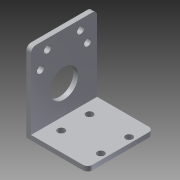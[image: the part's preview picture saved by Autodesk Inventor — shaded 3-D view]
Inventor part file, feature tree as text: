
AUTODESK INVENTOR PART (.ipt)
format: ipt  version: 2013 (Build 170138000, 138)  size: 143,872 bytes
history: native  units: in
note: dims shown in document units (in); Inventor stores cm internally (conversion verified against a paired STEP export)
features: extrude x3, sketch x3, fillet x1
ambient origin geometry x8: Origin, YZ Plane, XZ Plane, XY Plane, X Axis, Y Axis, Z Axis, Center Point
bodies: Solid1 (feature_tree)
feature tree (7):
  extrude  "Extrusion1"  Depth=2.5in
  extrude  "Extrusion2"  Depth=1.75in TaperAngle=0.0deg
  extrude  "Extrusion3"  Depth=0.625in
  fillet  "Fillet1"  Radius=0.1875in
  sketch  "Sketch1"  dims[d0=2.0in d1=2.5in]
  sketch  "Sketch2"  dims[d2=0.125in d3=1.75in d4=0.0in]
  sketch  "Sketch3"  dims[d5=0.875in d6=0.625in d7=0.1875in d8=0.1875in d9=1.5in d10=0.0in d11=0.75in d12=0.875in d13=0.75in d17=0.1875in d18=0.425in d19=1.0in d20=0.0in d21=1.625in d22=0.7874in d24=1.05in d25=0.3937in d27=1.0in d29=0.125in d30=0.375in d31=0.625in d32=1.25in]
